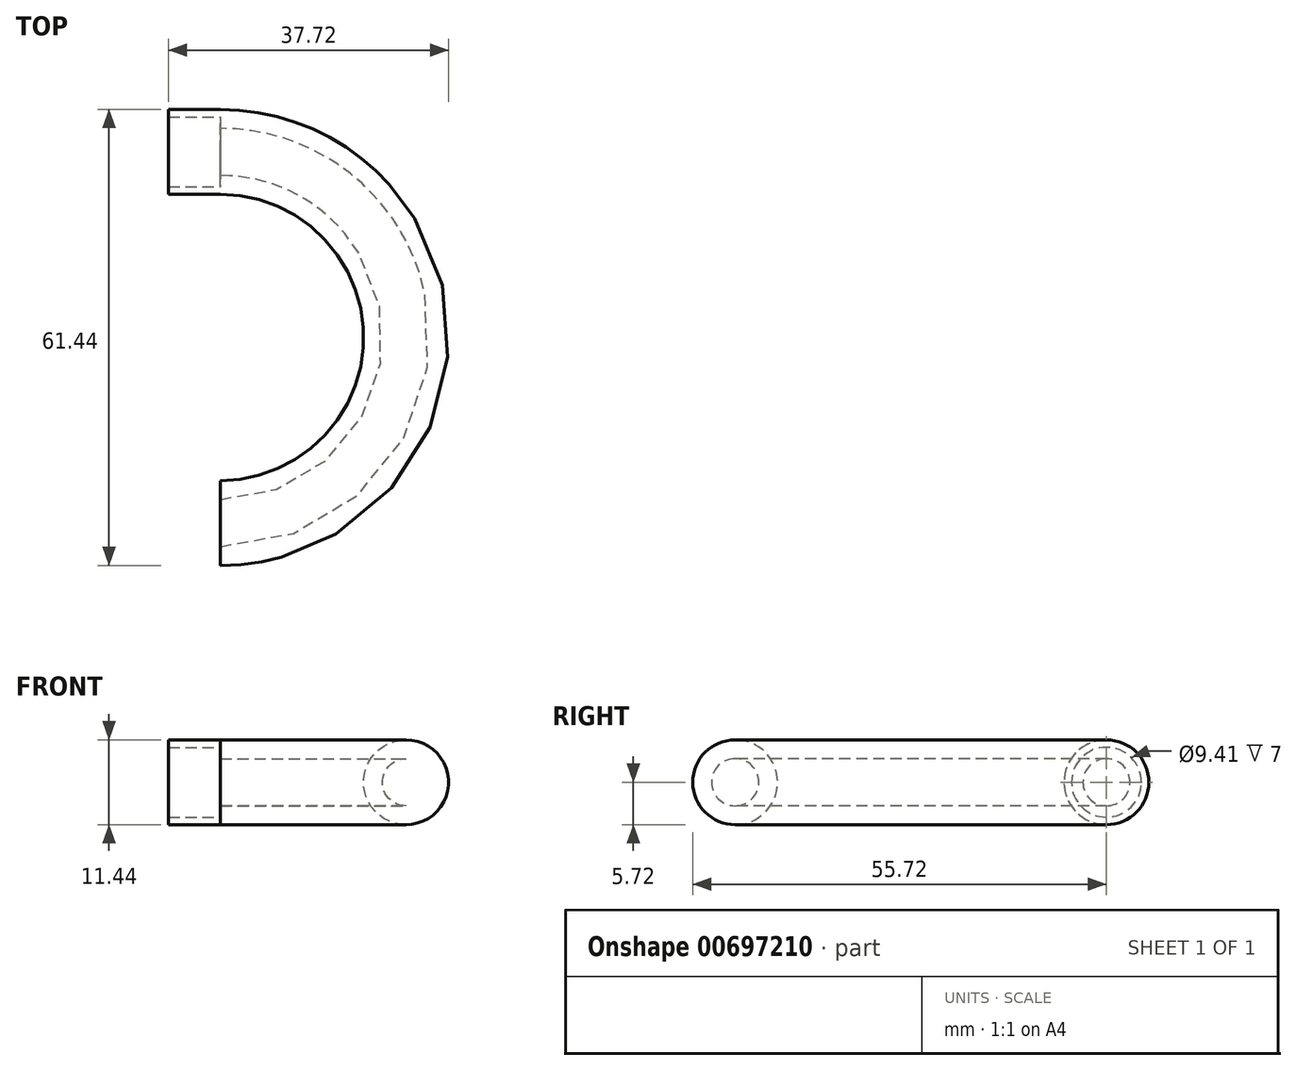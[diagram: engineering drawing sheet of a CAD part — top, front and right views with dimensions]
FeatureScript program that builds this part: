
annotation { "Feature Type Name" : "Feature", "Feature Type Description" : "" }
export const myFeature = defineFeature(function(context is Context, id is Id, definition is map)
    precondition{}
    {
        {
            var Q0;
            Q0=qCreatedBy(makeId("Top.planeOp"),FACE);
            var sketch = newSketch(context, id + "F0", { "sketchPlane" : qUnion([Q0])});
            skArc(sketch, "E0", {"start": v(0, 25) * mm, "mid": v(25, 0) * mm, "end": v(0, -25) * mm});
            skSolve(sketch);
        }
        {
            var Q0;
            Q0=qCreatedBy(makeId("Right.planeOp"),FACE);
            var sketch = newSketch(context, id + "F1", { "sketchPlane" : qUnion([Q0])});
            skCircle(sketch, "E1", {"center": v(25, 0) * mm, "radius": 3.17 * mm});
            skCircle(sketch, "E2", {"center": v(25, 0) * mm, "radius": 5.71 * mm});
            skSolve(sketch);
        }
        {
            var Q0;
            Q0=makeQuery(id+"F1.imprint","IMPRINT",FACE,{"disambiguationData":[TD([[makeQuery(id+"F1.imprint","IMPRINT",EDGE,{"derivedFrom":sQuery(id+"F1.wireOp",EDGE,"E1")}),-1.0]])]});
            var Q1;
            Q1=sQuery(id+"F0.wireOp",EDGE,"E0");
            sweep(context, id + "F2", {"profiles" : qUnion([Q0]), "path" : qUnion([Q1])});
        }
        {
            var Q0;
            Q0=makeQuery(id+"F2.opSweep","CAP_FACE",FACE,{"disambiguationData":[OSD([sQuery(id+"F0.wireOp",VERTEX,"E0.start"),sQuery(id+"F1.wireOp",EDGE,"E1"),sQuery(id+"F1.wireOp",EDGE,"E2")])],"isStart":true});
            var sketch = newSketch(context, id + "F3", { "sketchPlane" : qUnion([Q0])});
            skCircle(sketch, "E3", {"center": v(-25, 0) * mm, "radius": 4.7 * mm});
            skCircle(sketch, "E4", {"center": v(-25, 0) * mm, "radius": 5.71 * mm});
            skCircle(sketch, "E5.MirrorC", {"center": v(25, 0) * mm, "radius": 5.71 * mm});
            skCircle(sketch, "E6.MirrorC", {"center": v(25, 0) * mm, "radius": 4.7 * mm});
            skSolve(sketch);
        }
        {
            var Q0;
            Q0=makeQuery(id+"F3.imprint","IMPRINT",FACE,{"disambiguationData":[TD([[makeQuery(id+"F3.imprint","IMPRINT",EDGE,{"derivedFrom":sQuery(id+"F3.wireOp",EDGE,"E5.MirrorC")}),-1.0]])]});
            var Q1;
            Q1=makeQuery(id+"F3.imprint","IMPRINT",FACE,{"disambiguationData":[TD([[makeQuery(id+"F3.imprint","IMPRINT",EDGE,{"derivedFrom":sQuery(id+"F3.wireOp",EDGE,"E3")}),-1.0]])]});
            extrude(context, id + "F4", {"entities" : qUnion([Q0, Q1]), "operationType" : NewBodyOperationType.ADD, "depth" : 7 * mm, "offsetDistance" : 25 * mm});
        }
    });
